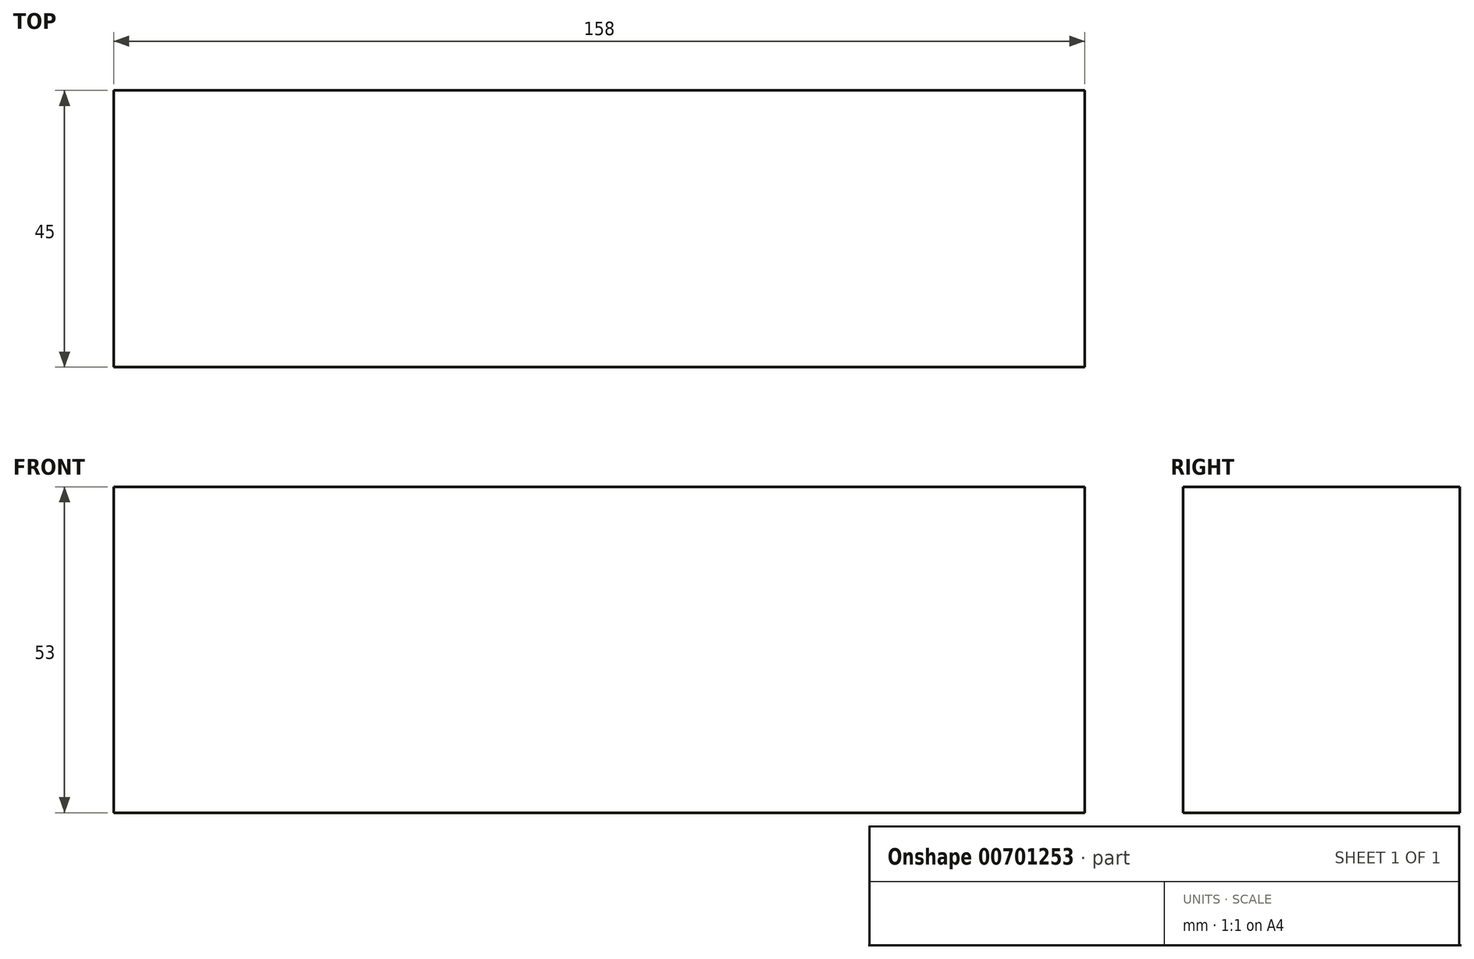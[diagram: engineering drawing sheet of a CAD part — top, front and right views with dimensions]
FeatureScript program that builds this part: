
annotation { "Feature Type Name" : "Feature", "Feature Type Description" : "" }
export const myFeature = defineFeature(function(context is Context, id is Id, definition is map)
    precondition{}
    {
        {
            var Q0;
            Q0=qCreatedBy(makeId("Front.planeOp"),FACE);
            var sketch = newSketch(context, id + "F0", { "sketchPlane" : qUnion([Q0])});
            skLineSegment(sketch, "E0.bottom", {"start": v(0, 0) * mm, "end": v(158, 0) * mm});
            skLineSegment(sketch, "E0.top", {"start": v(0, 53) * mm, "end": v(158, 53) * mm});
            skLineSegment(sketch, "E0.left", {"start": v(0, 0) * mm, "end": v(0, 53) * mm});
            skLineSegment(sketch, "E0.right", {"start": v(158, 0) * mm, "end": v(158, 53) * mm});
            skSolve(sketch);
        }
        {
            var Q0;
            Q0=makeQuery(id+"F0.imprint","IMPRINT",FACE,{"disambiguationData":[TD([[makeQuery(id+"F0.imprint","IMPRINT",EDGE,{"derivedFrom":sQuery(id+"F0.wireOp",EDGE,"E0.bottom")}),1.0]])]});
            extrude(context, id + "F1", {"entities" : qUnion([Q0]), "depth" : 45 * mm, "offsetDistance" : 25 * mm});
        }
    });
